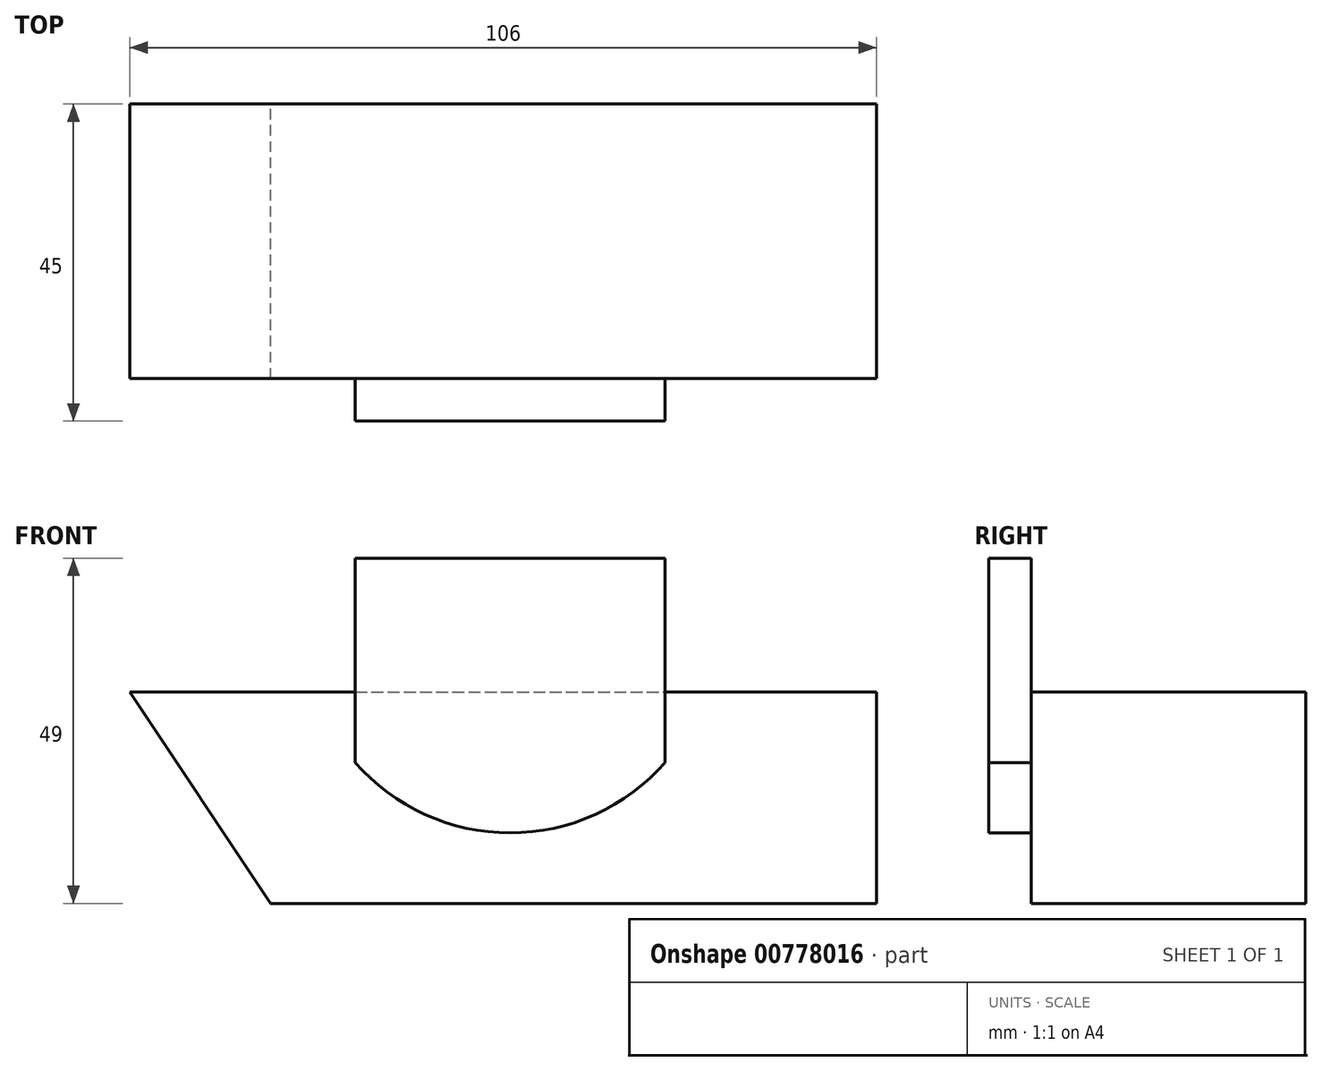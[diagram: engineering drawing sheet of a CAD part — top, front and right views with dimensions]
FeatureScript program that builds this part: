
annotation { "Feature Type Name" : "Feature", "Feature Type Description" : "" }
export const myFeature = defineFeature(function(context is Context, id is Id, definition is map)
    precondition{}
    {
        {
            var Q0;
            Q0=qCreatedBy(makeId("Front.planeOp"),FACE);
            var sketch = newSketch(context, id + "F0", { "sketchPlane" : qUnion([Q0])});
            skLineSegment(sketch, "E0", {"start": v(0, 0) * mm, "end": v(0, -30) * mm});
            skLineSegment(sketch, "E1", {"start": v(0, -30) * mm, "end": v(-86, -30) * mm});
            skLineSegment(sketch, "E2", {"start": v(-86, -30) * mm, "end": v(-106, 0) * mm});
            skLineSegment(sketch, "E3", {"start": v(-106, 0) * mm, "end": v(0, 0) * mm});
            skSolve(sketch);
        }
        {
            var Q0;
            Q0=makeQuery(id+"F0.imprint","IMPRINT",FACE,{"disambiguationData":[TD([[makeQuery(id+"F0.imprint","IMPRINT",EDGE,{"derivedFrom":sQuery(id+"F0.wireOp",EDGE,"E0")}),-1.0]])]});
            extrude(context, id + "F1", {"entities" : qUnion([Q0]), "depth" : (78 / 2) * mm, "offsetDistance" : 25 * mm});
        }
        {
            var Q0;
            Q0=makeQuery(id+"F1.opExtrude","CAP_FACE",FACE,{"disambiguationData":[OSD([sQuery(id+"F0.wireOp",EDGE,"E0"),sQuery(id+"F0.wireOp",EDGE,"E1"),sQuery(id+"F0.wireOp",EDGE,"E2"),sQuery(id+"F0.wireOp",EDGE,"E3")])],"isStart":false});
            var sketch = newSketch(context, id + "F2", { "sketchPlane" : qUnion([Q0])});
            skLineSegment(sketch, "E4", {"start": v(-74, -10) * mm, "end": v(-74, 19) * mm});
            skLineSegment(sketch, "E5", {"start": v(-74, 19) * mm, "end": v(-30, 19) * mm});
            skLineSegment(sketch, "E6", {"start": v(-30, 19) * mm, "end": v(-30, -10) * mm});
            skArc(sketch, "E7", {"start": v(-74, -10) * mm, "mid": v(-52, -20) * mm, "end": v(-30, -10) * mm});
            skPoint(sketch, "E8", {"position": v(-52, -20) * mm});
            skSolve(sketch);
        }
        {
            var Q0;
            Q0 = qSketchRegion(id + "F2", true);
            extrude(context, id + "F3", {"entities" : qUnion([Q0]), "operationType" : NewBodyOperationType.ADD, "depth" : 6 * mm, "offsetDistance" : 25 * mm});
        }
    });
